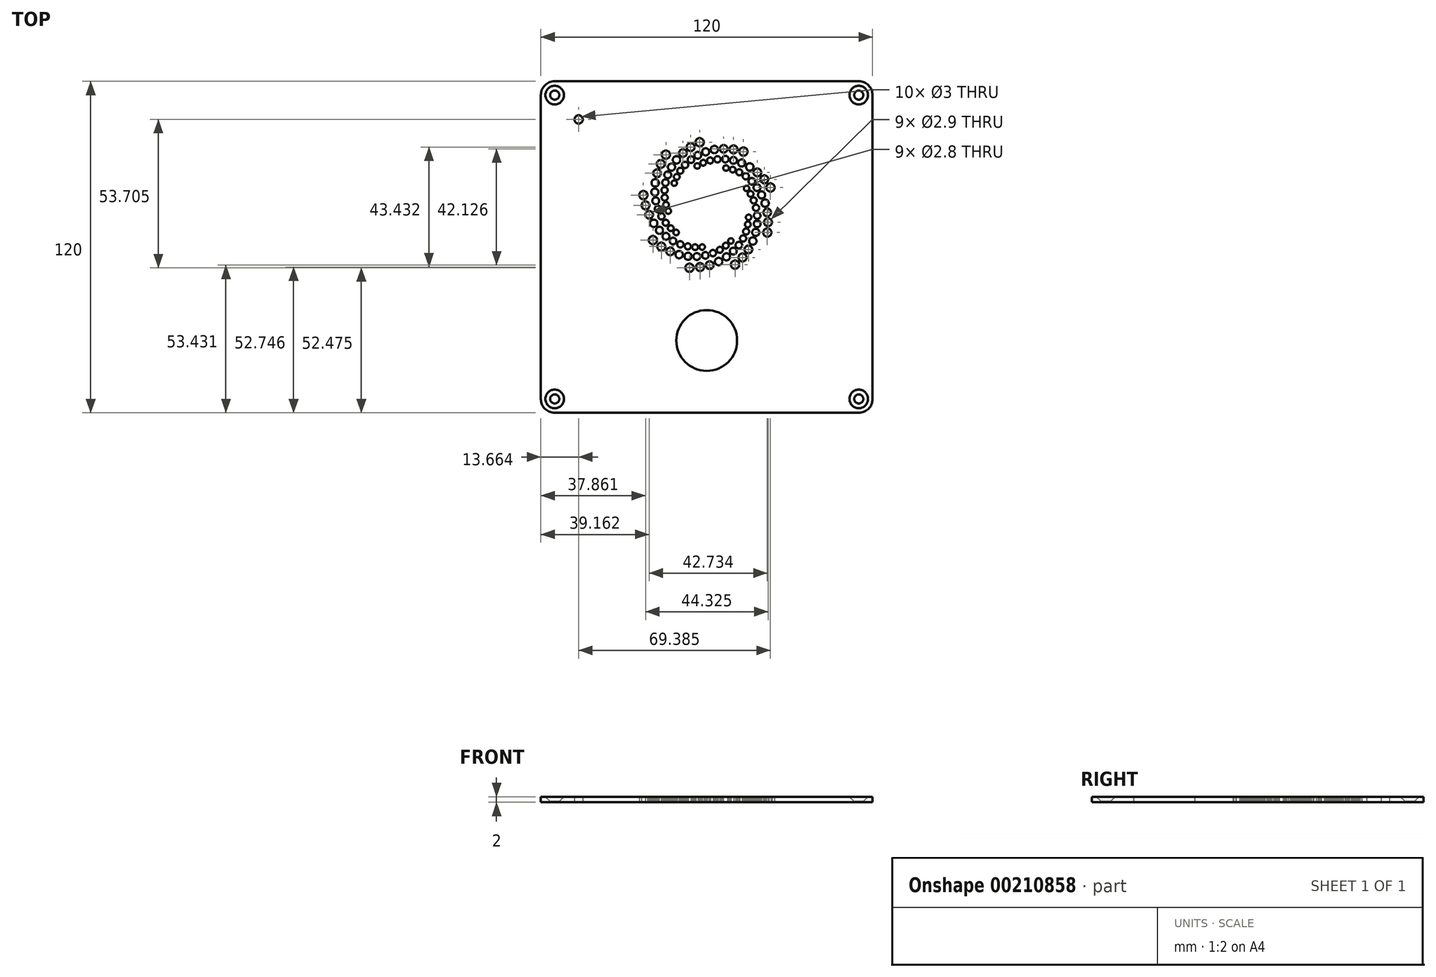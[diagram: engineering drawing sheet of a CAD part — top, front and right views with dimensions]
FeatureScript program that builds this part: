
annotation { "Feature Type Name" : "Feature", "Feature Type Description" : "" }
export const myFeature = defineFeature(function(context is Context, id is Id, definition is map)
    precondition{}
    {
        {
            var Q0;
            Q0=qCreatedBy(makeId("Top.planeOp"),FACE);
            var sketch = newSketch(context, id + "F0", { "sketchPlane" : qUnion([Q0])});
            skPoint(sketch, "E0.middle", {"position": v(0, 0) * mm});
            skLineSegment(sketch, "E1.bottom", {"start": v(55, -60) * mm, "end": v(-55, -60) * mm});
            skLineSegment(sketch, "E1.top", {"start": v(55, 60) * mm, "end": v(-55, 60) * mm});
            skLineSegment(sketch, "E1.left", {"start": v(60, -55) * mm, "end": v(60, 55) * mm});
            skLineSegment(sketch, "E1.right", {"start": v(-60, -55) * mm, "end": v(-60, 55) * mm});
            skPoint(sketch, "E2.visualSharp", {"position": v(-60, 60) * mm});
            skArc(sketch, "E2.filletArc", {"start": v(-55, 60) * mm, "mid": v(-58.54, 58.54) * mm, "end": v(-60, 55) * mm});
            skPoint(sketch, "E3.visualSharp", {"position": v(60, 60) * mm});
            skArc(sketch, "E3.filletArc", {"start": v(60, 55) * mm, "mid": v(58.54, 58.54) * mm, "end": v(55, 60) * mm});
            skPoint(sketch, "E4.visualSharp", {"position": v(60, -60) * mm});
            skArc(sketch, "E4.filletArc", {"start": v(55, -60) * mm, "mid": v(58.54, -58.54) * mm, "end": v(60, -55) * mm});
            skPoint(sketch, "E5.visualSharp", {"position": v(-60, -60) * mm});
            skArc(sketch, "E5.filletArc", {"start": v(-60, -55) * mm, "mid": v(-58.54, -58.54) * mm, "end": v(-55, -60) * mm});
            skCircle(sketch, "E6", {"center": v(0, -33.86) * mm, "radius": 11 * mm});
            skCircle(sketch, "E7", {"center": v(-2.54, 37.93) * mm, "radius": 1.5 * mm});
            skCircle(sketch, "E8", {"center": v(13.29, 34.54) * mm, "radius": 1.5 * mm});
            skCircle(sketch, "E9", {"center": v(-14.77, 33.42) * mm, "radius": 1.5 * mm});
            skCircle(sketch, "E10", {"center": v(-22.91, 18.78) * mm, "radius": 1.5 * mm});
            skCircle(sketch, "E11", {"center": v(-5.81, 36.18) * mm, "radius": 1.45 * mm});
            skCircle(sketch, "E12", {"center": v(-16.64, 30.07) * mm, "radius": 1.45 * mm});
            skCircle(sketch, "E13", {"center": v(9.7, 35.34) * mm, "radius": 1.45 * mm});
            skCircle(sketch, "E14", {"center": v(-22.14, 15.07) * mm, "radius": 1.45 * mm});
            skCircle(sketch, "E15", {"center": v(-8.6, 34.03) * mm, "radius": 1.4 * mm});
            skCircle(sketch, "E16", {"center": v(6.15, 35.56) * mm, "radius": 1.4 * mm});
            skCircle(sketch, "E17", {"center": v(-17.95, 26.7) * mm, "radius": 1.4 * mm});
            skCircle(sketch, "E18", {"center": v(-20.84, 11.68) * mm, "radius": 1.4 * mm});
            skCircle(sketch, "E19", {"center": v(-10.92, 31.56) * mm, "radius": 1.35 * mm});
            skCircle(sketch, "E20", {"center": v(2.77, 35.28) * mm, "radius": 1.35 * mm});
            skCircle(sketch, "E21", {"center": v(-18.63, 23.23) * mm, "radius": 1.35 * mm});
            skCircle(sketch, "E22", {"center": v(-19.19, 8.58) * mm, "radius": 1.35 * mm});
            skCircle(sketch, "E23", {"center": v(-18.76, 19.88) * mm, "radius": 1.3 * mm});
            skCircle(sketch, "E24", {"center": v(-12.72, 28.92) * mm, "radius": 1.3 * mm});
            skCircle(sketch, "E25", {"center": v(-0.37, 34.45) * mm, "radius": 1.3 * mm});
            skCircle(sketch, "E26", {"center": v(-17.09, 6.02) * mm, "radius": 1.3 * mm});
            skCircle(sketch, "E27", {"center": v(-3.24, 33.2) * mm, "radius": 1.25 * mm});
            skCircle(sketch, "E28", {"center": v(-14.09, 26.13) * mm, "radius": 1.25 * mm});
            skCircle(sketch, "E29", {"center": v(-18.44, 16.7) * mm, "radius": 1.25 * mm});
            skCircle(sketch, "E30", {"center": v(-14.74, 3.87) * mm, "radius": 1.25 * mm});
            skCircle(sketch, "E31", {"center": v(-5.7, 31.61) * mm, "radius": 1.2 * mm});
            skCircle(sketch, "E32", {"center": v(-14.91, 23.3) * mm, "radius": 1.2 * mm});
            skCircle(sketch, "E33", {"center": v(-17.61, 13.76) * mm, "radius": 1.2 * mm});
            skCircle(sketch, "E34", {"center": v(-12.18, 2.16) * mm, "radius": 1.2 * mm});
            skCircle(sketch, "E35", {"center": v(-7.82, 29.73) * mm, "radius": 1.15 * mm});
            skCircle(sketch, "E36", {"center": v(-15.27, 20.57) * mm, "radius": 1.15 * mm});
            skCircle(sketch, "E37", {"center": v(-16.38, 11.1) * mm, "radius": 1.15 * mm});
            skCircle(sketch, "E38", {"center": v(-9.54, 0.98) * mm, "radius": 1.15 * mm});
            skCircle(sketch, "E39", {"center": v(-9.55, 27.62) * mm, "radius": 1.1 * mm});
            skCircle(sketch, "E40", {"center": v(-15.2, 17.87) * mm, "radius": 1.1 * mm});
            skCircle(sketch, "E41", {"center": v(-14.83, 8.79) * mm, "radius": 1.1 * mm});
            skCircle(sketch, "E42", {"center": v(-6.83, 0.22) * mm, "radius": 1.1 * mm});
            skCircle(sketch, "E43", {"center": v(-10.83, 25.4) * mm, "radius": 1.05 * mm});
            skCircle(sketch, "E44", {"center": v(-14.71, 15.3) * mm, "radius": 1.05 * mm});
            skCircle(sketch, "E45", {"center": v(-13, 6.79) * mm, "radius": 1.05 * mm});
            skCircle(sketch, "E46", {"center": v(-4.2, -0.06) * mm, "radius": 1.05 * mm});
            skCircle(sketch, "E47", {"center": v(-11.74, 23.12) * mm, "radius": 1 * mm});
            skCircle(sketch, "E48", {"center": v(-13.91, 13.01) * mm, "radius": 1 * mm});
            skCircle(sketch, "E49", {"center": v(-11.06, 5.25) * mm, "radius": 1 * mm});
            skCircle(sketch, "E50", {"center": v(-1.64, 0) * mm, "radius": 1 * mm});
            skCircle(sketch, "E51", {"center": v(21.92, 5.25) * mm, "radius": 1.5 * mm});
            skCircle(sketch, "E52", {"center": v(10.28, -6.39) * mm, "radius": 1.5 * mm});
            skCircle(sketch, "E53", {"center": v(23.05, 21.54) * mm, "radius": 1.5 * mm});
            skCircle(sketch, "E54", {"center": v(-19.45, 2.5) * mm, "radius": 1.5 * mm});
            skCircle(sketch, "E55", {"center": v(-6.22, -7.52) * mm, "radius": 1.5 * mm});
            skCircle(sketch, "E56", {"center": v(22.19, 8.98) * mm, "radius": 1.45 * mm});
            skCircle(sketch, "E57", {"center": v(20.84, 24.51) * mm, "radius": 1.45 * mm});
            skCircle(sketch, "E58", {"center": v(-16.42, 0.15) * mm, "radius": 1.45 * mm});
            skCircle(sketch, "E59", {"center": v(-2.42, -7.25) * mm, "radius": 1.45 * mm});
            skCircle(sketch, "E60", {"center": v(12.95, -3.79) * mm, "radius": 1.45 * mm});
            skCircle(sketch, "E61", {"center": v(-13.2, -1.6) * mm, "radius": 1.4 * mm});
            skCircle(sketch, "E62", {"center": v(15.09, -0.87) * mm, "radius": 1.4 * mm});
            skCircle(sketch, "E63", {"center": v(1.09, -6.57) * mm, "radius": 1.4 * mm});
            skCircle(sketch, "E64", {"center": v(21.9, 12.53) * mm, "radius": 1.4 * mm});
            skCircle(sketch, "E65", {"center": v(18.31, 27) * mm, "radius": 1.4 * mm});
            skCircle(sketch, "E66", {"center": v(15.57, 28.99) * mm, "radius": 1.35 * mm});
            skCircle(sketch, "E67", {"center": v(21.13, 15.87) * mm, "radius": 1.35 * mm});
            skCircle(sketch, "E68", {"center": v(-9.97, -2.74) * mm, "radius": 1.35 * mm});
            skCircle(sketch, "E69", {"center": v(4.32, -5.26) * mm, "radius": 1.35 * mm});
            skCircle(sketch, "E70", {"center": v(16.67, 2.16) * mm, "radius": 1.35 * mm});
            skCircle(sketch, "E71", {"center": v(12.65, 30.41) * mm, "radius": 1.3 * mm});
            skCircle(sketch, "E72", {"center": v(9.67, 31.38) * mm, "radius": 1.25 * mm});
            skCircle(sketch, "E73", {"center": v(6.73, 31.8) * mm, "radius": 1.2 * mm});
            skCircle(sketch, "E74", {"center": v(3.9, 31.76) * mm, "radius": 1.15 * mm});
            skCircle(sketch, "E75", {"center": v(1.25, 31.33) * mm, "radius": 1.1 * mm});
            skCircle(sketch, "E76", {"center": v(-1.25, 30.51) * mm, "radius": 1.05 * mm});
            skCircle(sketch, "E77", {"center": v(-3.42, 29.36) * mm, "radius": 1 * mm});
            skCircle(sketch, "E78", {"center": v(19.86, 18.87) * mm, "radius": 1.3 * mm});
            skCircle(sketch, "E79", {"center": v(18.2, 21.5) * mm, "radius": 1.25 * mm});
            skCircle(sketch, "E80", {"center": v(16.3, 23.8) * mm, "radius": 1.2 * mm});
            skCircle(sketch, "E81", {"center": v(14.14, 25.62) * mm, "radius": 1.15 * mm});
            skCircle(sketch, "E82", {"center": v(11.8, 27.05) * mm, "radius": 1.1 * mm});
            skCircle(sketch, "E83", {"center": v(9.39, 28.02) * mm, "radius": 1.05 * mm});
            skCircle(sketch, "E84", {"center": v(6.99, 28.6) * mm, "radius": 1 * mm});
            skCircle(sketch, "E85", {"center": v(17.74, 5.31) * mm, "radius": 1.3 * mm});
            skCircle(sketch, "E86", {"center": v(18.25, 8.4) * mm, "radius": 1.25 * mm});
            skCircle(sketch, "E87", {"center": v(18.25, 11.38) * mm, "radius": 1.2 * mm});
            skCircle(sketch, "E88", {"center": v(17.85, 14.18) * mm, "radius": 1.15 * mm});
            skCircle(sketch, "E89", {"center": v(17, 16.87) * mm, "radius": 1.1 * mm});
            skCircle(sketch, "E90", {"center": v(15.85, 19.21) * mm, "radius": 1.05 * mm});
            skCircle(sketch, "E91", {"center": v(14.42, 21.22) * mm, "radius": 1 * mm});
            skCircle(sketch, "E92", {"center": v(7.16, -3.55) * mm, "radius": 1.3 * mm});
            skCircle(sketch, "E93", {"center": v(9.62, -1.5) * mm, "radius": 1.25 * mm});
            skCircle(sketch, "E94", {"center": v(11.62, 0.68) * mm, "radius": 1.2 * mm});
            skCircle(sketch, "E95", {"center": v(13.16, 3.08) * mm, "radius": 1.15 * mm});
            skCircle(sketch, "E96", {"center": v(14.25, 5.6) * mm, "radius": 1.1 * mm});
            skCircle(sketch, "E97", {"center": v(14.88, 8.17) * mm, "radius": 1.05 * mm});
            skCircle(sketch, "E98", {"center": v(15.17, 10.75) * mm, "radius": 1 * mm});
            skCircle(sketch, "E99", {"center": v(-6.74, -3.35) * mm, "radius": 1.3 * mm});
            skCircle(sketch, "E100", {"center": v(-3.57, -3.44) * mm, "radius": 1.25 * mm});
            skCircle(sketch, "E101", {"center": v(-0.48, -3.03) * mm, "radius": 1.2 * mm});
            skCircle(sketch, "E102", {"center": v(2.24, -2.21) * mm, "radius": 1.15 * mm});
            skCircle(sketch, "E103", {"center": v(4.74, -1.03) * mm, "radius": 1.1 * mm});
            skCircle(sketch, "E104", {"center": v(6.92, 0.51) * mm, "radius": 1.05 * mm});
            skCircle(sketch, "E105", {"center": v(8.74, 2.2) * mm, "radius": 1 * mm});
            skCircle(sketch, "E106", {"center": v(-46.34, 46.18) * mm, "radius": 1.5 * mm});
            skSolve(sketch);
        }
        {
            var Q0;
            Q0=makeQuery(id+"F0.imprint","IMPRINT",FACE,{"disambiguationData":[TD([[makeQuery(id+"F0.imprint","IMPRINT",EDGE,{"derivedFrom":sQuery(id+"F0.wireOp",EDGE,"E1.bottom")}),-1.0]])]});
            extrude(context, id + "F1", {"entities" : qUnion([Q0]), "depth" : 2 * mm});
        }
        {
            var Q0;
            Q0=makeQuery(id+"F1.opExtrude","CAP_FACE",FACE,{"disambiguationData":[OSD([sQuery(id+"F0.wireOp",EDGE,"E1.bottom"),sQuery(id+"F0.wireOp",EDGE,"E1.top"),sQuery(id+"F0.wireOp",EDGE,"E1.left"),sQuery(id+"F0.wireOp",EDGE,"E1.right"),sQuery(id+"F0.wireOp",EDGE,"E2.filletArc"),sQuery(id+"F0.wireOp",EDGE,"E3.filletArc"),sQuery(id+"F0.wireOp",EDGE,"E4.filletArc"),sQuery(id+"F0.wireOp",EDGE,"E5.filletArc")])],"isStart":false});
            var sketch = newSketch(context, id + "F2", { "sketchPlane" : qUnion([Q0])});
            skLineSegment(sketch, "E107.bottom", {"start": v(55, -55) * mm, "end": v(-55, -55) * mm});
            skLineSegment(sketch, "E107.top", {"start": v(55, 55) * mm, "end": v(-55, 55) * mm});
            skLineSegment(sketch, "E107.left", {"start": v(55, -55) * mm, "end": v(55, 55) * mm});
            skLineSegment(sketch, "E107.right", {"start": v(-55, -55) * mm, "end": v(-55, 55) * mm});
            skPoint(sketch, "E107.middle", {"position": v(0, 0) * mm});
            skSolve(sketch);
        }
        {
            var Q0;
            Q0=sQuery(id+"F2.wireOp",VERTEX,"E107.top.end");
            var Q1;
            Q1=sQuery(id+"F2.wireOp",VERTEX,"E107.left.end");
            var Q2;
            Q2=sQuery(id+"F2.wireOp",VERTEX,"E107.left.start");
            var Q3;
            Q3=sQuery(id+"F2.wireOp",VERTEX,"E107.right.start");
            var Q4;
            Q4=makeQuery(id+"F1.opExtrude","SWEPT_BODY",BODY,{"disambiguationData":[OSD([sQuery(id+"F0.wireOp",EDGE,"E1.bottom"),sQuery(id+"F0.wireOp",EDGE,"E1.top"),sQuery(id+"F0.wireOp",EDGE,"E1.left"),sQuery(id+"F0.wireOp",EDGE,"E1.right"),sQuery(id+"F0.wireOp",EDGE,"E2.filletArc"),sQuery(id+"F0.wireOp",EDGE,"E3.filletArc"),sQuery(id+"F0.wireOp",EDGE,"E4.filletArc"),sQuery(id+"F0.wireOp",EDGE,"E5.filletArc")])]});
            hole(context, id + "F3", {"style" : HoleStyle.C_SINK, "endStyle" : HoleEndStyle.THROUGH, "standardTappedOrClearance" : lookupTablePath({ "standard" : "ISO", "fit" : "Normal", "size" : "M3", "type" : "Clearance" }), "standardBlindInLast" : lookupTablePath({ "fit" : "Standard", "standard" : "ISO", "size" : "M3", "type" : "Clearance" }), "holeDiameter" : 3.3 * mm, "cSinkDiameter" : 6.72 * mm, "cSinkAngle" : 90 * degree, "locations" : qUnion([Q0, Q1, Q2, Q3]), "scope" : qUnion([Q4]), "majorDiameter" : 3 * mm, "tappedDepth" : 12 * mm, "tapClearance" : 3});
        }
    });
